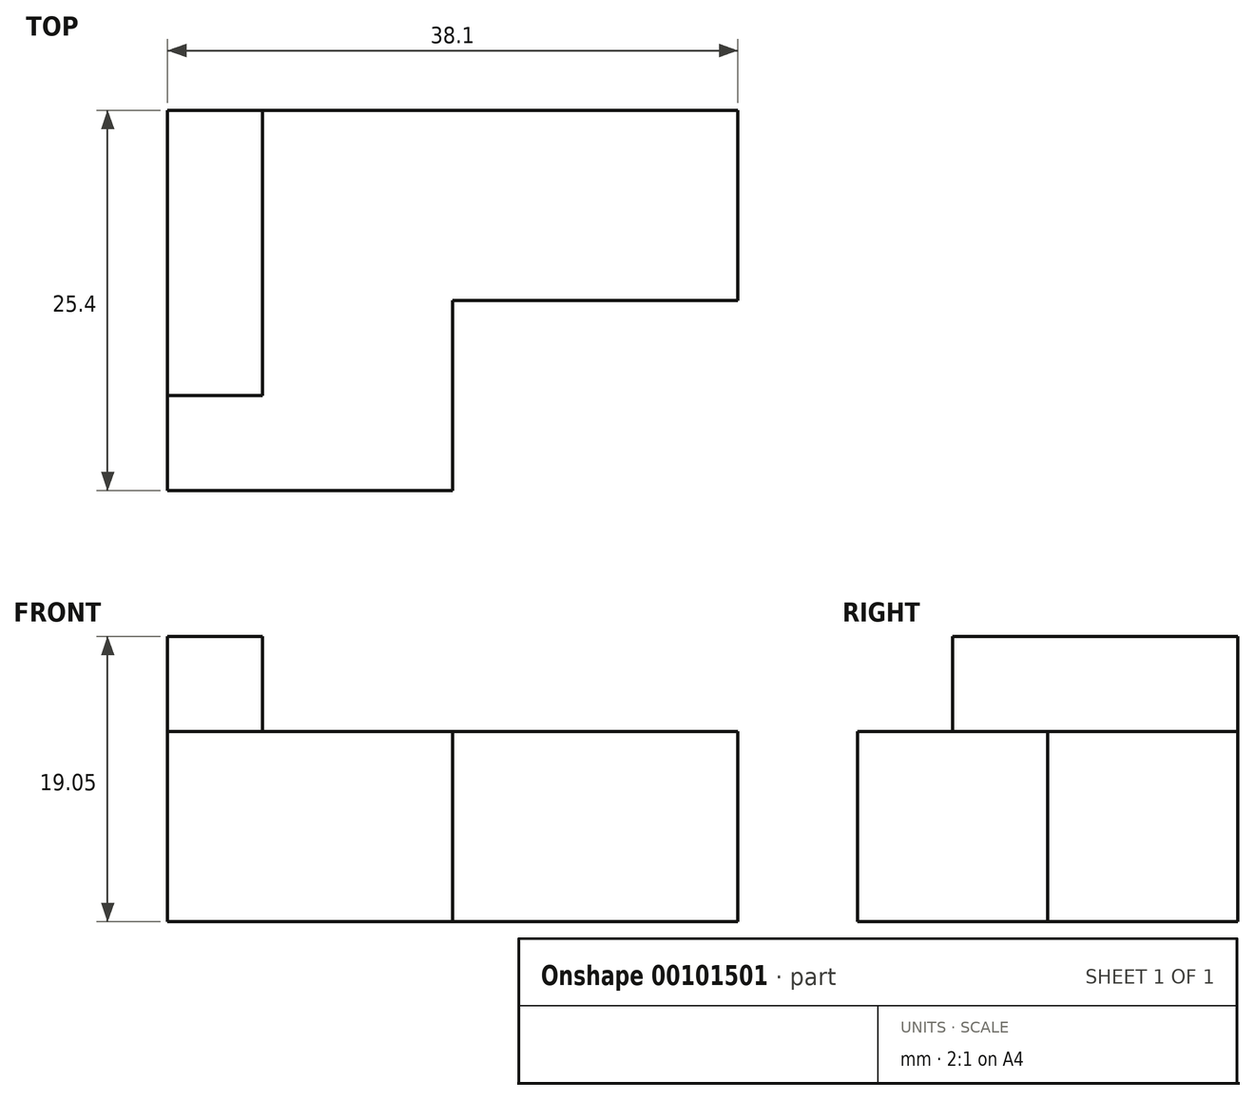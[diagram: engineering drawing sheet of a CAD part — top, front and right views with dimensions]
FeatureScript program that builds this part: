
annotation { "Feature Type Name" : "Feature", "Feature Type Description" : "" }
export const myFeature = defineFeature(function(context is Context, id is Id, definition is map)
    precondition{}
    {
        {
            var Q0;
            Q0=qCreatedBy(makeId("Top.planeOp"),FACE);
            var sketch = newSketch(context, id + "F0", { "sketchPlane" : qUnion([Q0])});
            skLineSegment(sketch, "E0", {"start": v(0, 0) * mm, "end": v(0, 25.4) * mm});
            skLineSegment(sketch, "E1", {"start": v(0, 25.4) * mm, "end": v(38.1, 25.4) * mm});
            skLineSegment(sketch, "E2", {"start": v(38.1, 25.4) * mm, "end": v(38.1, 12.7) * mm});
            skLineSegment(sketch, "E3", {"start": v(38.1, 12.7) * mm, "end": v(19.05, 12.7) * mm});
            skLineSegment(sketch, "E4", {"start": v(19.05, 12.7) * mm, "end": v(19.05, 0) * mm});
            skLineSegment(sketch, "E5", {"start": v(19.05, 0) * mm, "end": v(0, 0) * mm});
            skSolve(sketch);
        }
        {
            var Q0;
            Q0 = qSketchRegion(id + "F0", true);
            extrude(context, id + "F1", {"entities" : qUnion([Q0]), "endBound" : BoundingType.SYMMETRIC, "depth" : 12.7 * mm});
        }
        {
            var Q0;
            Q0=qCreatedBy(makeId("Top.planeOp"),FACE);
            var sketch = newSketch(context, id + "F2", { "sketchPlane" : qUnion([Q0])});
            skLineSegment(sketch, "E6.bottom", {"start": v(0, 25.4) * mm, "end": v(6.35, 25.4) * mm});
            skLineSegment(sketch, "E6.top", {"start": v(0, 6.35) * mm, "end": v(6.35, 6.35) * mm});
            skLineSegment(sketch, "E6.left", {"start": v(0, 25.4) * mm, "end": v(0, 6.35) * mm});
            skLineSegment(sketch, "E6.right", {"start": v(6.35, 25.4) * mm, "end": v(6.35, 6.35) * mm});
            skSolve(sketch);
        }
        {
            var Q0;
            Q0 = qSketchRegion(id + "F2", true);
            extrude(context, id + "F3", {"entities" : qUnion([Q0]), "operationType" : NewBodyOperationType.ADD, "depth" : 12.7 * mm});
        }
    });
